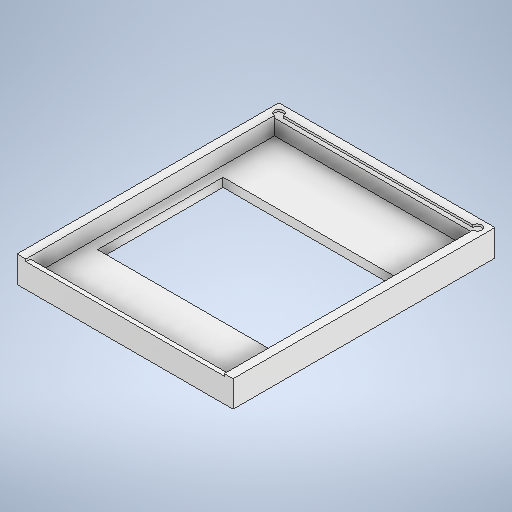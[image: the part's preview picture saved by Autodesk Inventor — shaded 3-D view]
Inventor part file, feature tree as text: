
AUTODESK INVENTOR PART (.ipt)
format: ipt  version: 2025 (Build 290162000, 162)  size: 372,224 bytes
history: native  units: in
note: dims shown in document units (in); Inventor stores cm internally (conversion verified against a paired STEP export)
features: extrude x6, sketch x6
ambient origin geometry x8: Origin, YZ Plane, XZ Plane, XY Plane, X Axis, Y Axis, Z Axis, Center Point
bodies: Solid1 (feature_tree)
feature tree (12):
  extrude  "Extrusion1"  Depth=1.9331in
  extrude  "Extrusion2"  Depth=0.0787in
  extrude  "Extrusion3"  Depth=0.0197in TaperAngle=0.0deg
  extrude  "Extrusion6"  Depth=0.1378in TaperAngle=0.0deg
  extrude  "Extrusion7"  Depth=1.5945in
  extrude  "Extrusion8"  Depth=0.0394in
  sketch  "Sketch1"  dims[d0=2.4606in d1=1.9331in]
  sketch  "Sketch2"  dims[d2=0.2362in d3=0.0in d4=0.0787in]
  sketch  "Sketch3"  dims[d5=0.0787in d6=0.0197in d7=0.0in]
  sketch  "Sketch8"  dims[d8=0.0394in d9=0.1378in d10=0.0in]
  sketch  "Sketch9"  dims[d28=1.122in d29=1.5945in]
  sketch  "Sketch10"  dims[d30=0.1248in d31=0.0in d32=0.0394in d33=0.0394in d34=0.0394in d35=0.0394in d36=2.2638in d37=0.0in d38=0.0in d39=0.0394in d40=0.3937in d41=0.0in]
